# Revit family: Faucet-Lavatory-KOHLER-ALEO-K-31237T_1
name_source: partatom
category: Plumbing Fixtures
units: mm (PartAtom-declared; Revit-internal decimal feet)

## family parameters
Cut with Voids When Loaded = No
Host = Face
OmniClass Number = 23.31.11.00
OmniClass Title = Faucets
Part Type = Normal
Room Calculation Point = No
Round Connector Dimension = Use Diameter
Shared = No

## types (6) — shared parameters
ADA Compliant = No
Assembly Code = D2010
CW Connection = Yes
Cold Water Inlet = Cold Water Inlet
Date Modified = 12/20/2022
Default Elevation = 36"
Flow Rate = 1 GPM
HW Connection = Yes
Handle Clearance = 2 3/16"
Height = 4 1/16"
Hot Water Inlet = Hot Water Inlet
Length = 3 15/16"
Manufacturer = Kohler Co.
Master Format 2014 = 22 41 39
Master Format 2014 Name = Residential Faucets, Supplies, and Trim
Material = Premium Metal Construction
Pressure = 60.00 psi
Product Name = ALEO
Spout Reach = 3 15/16"
URL = http://www.kohler.com.cn
Vent Connection = No
Waste Connection = No
Waste Water Outlet = Waste Water Outlet
WaterSense Certified = No

## per-type parameters (varying)
| type | 4 | 4ND | Description | Drain Included | Finish | Model | Product Documentation Link | Product Page URL | Type |
| CP-Polished Chrome | Yes | No | 8 Basin Faucet (Smart Style) | Yes | Kohler-Metal-CP-Polished_Chrome | K-31237T-4-CP | https://files.kohler.com.cn | https://www.kohler.com.cn | 1 |
| 2BL-Black | Yes | No | 8 Basin Faucet (Smart Style) | Yes | KOHLER-Metal-2BL-Black | K-31237T-4-2BL | https://files.kohler.com.cn | https://www.kohler.com.cn | 2 |
| BL-Matte Black | Yes | No | 8 Basin Faucet (Smart Style) | Yes | Kohler-Metal-BL-Matte_Black | K-31237T-4-BL | https://files.kohler.com.cn |  | 3 |
| No Drain, BL-Matte Black | No | Yes | S Wide Spread Lavatory Faucet | No | Kohler-Metal-BL-Matte_Black | K-31237T-4ND-BL |  |  | 4 |
| No Drain, BN-Vibrant Brushed Nickel | No | Yes | S Wide Spread Lavatory Faucet | No | Kohler-Metal-BN-Vibrant_Brushed_Nickel | K-31237T-4ND-BN |  |  | 5 |
| No Drain, CP-Polished Chrome | No | Yes | S Wide Spread Lavatory Faucet | No | Kohler-Metal-CP-Polished_Chrome | K-31237T-4ND-CP |  |  | 6 |

## geometry (parser evidence)
native form markers: Sweep x9
no freeform markers — native parametric forms only
